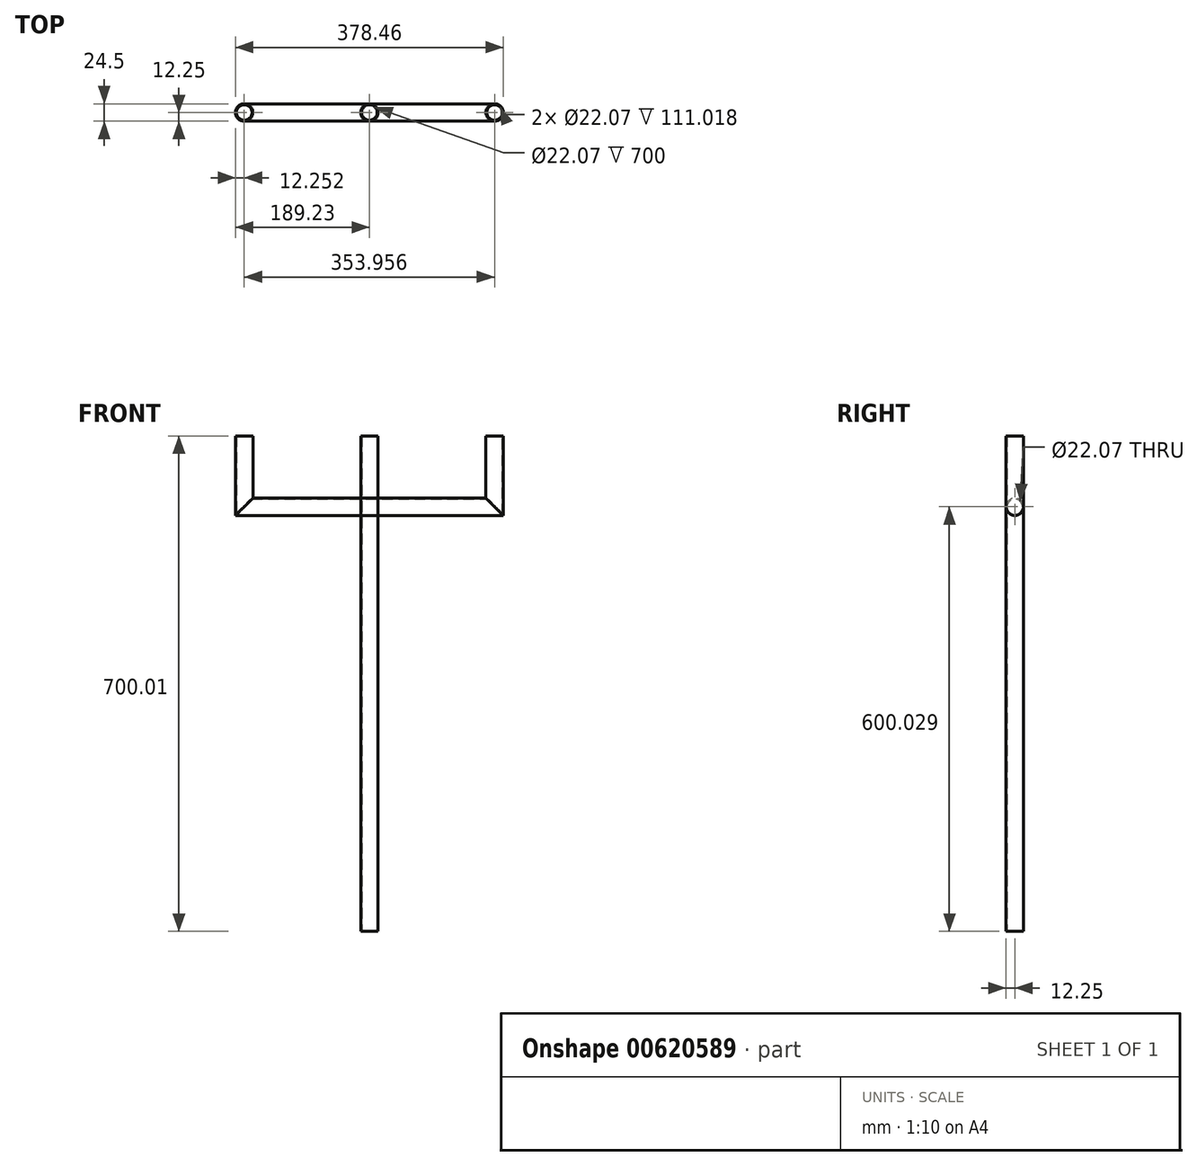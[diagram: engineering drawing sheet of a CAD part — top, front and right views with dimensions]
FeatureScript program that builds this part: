
annotation { "Feature Type Name" : "Feature", "Feature Type Description" : "" }
export const myFeature = defineFeature(function(context is Context, id is Id, definition is map)
    precondition{}
    {
        {
            var Q0;
            Q0=qCreatedBy(makeId("Top.planeOp"),FACE);
            var sketch = newSketch(context, id + "F0", { "sketchPlane" : qUnion([Q0])});
            skCircle(sketch, "E0", {"center": v(0, 0) * mm, "radius": 12.25 * mm});
            skCircle(sketch, "E1", {"center": v(0, 0) * mm, "radius": 11.03 * mm});
            skSolve(sketch);
        }
        {
            var Q0;
            Q0 = qSketchRegion(id + "F0", true);
            extrude(context, id + "F1", {"entities" : qUnion([Q0]), "depth" : 700 * mm, "offsetDistance" : 25 * mm});
        }
        {
            var Q0;
            Q0=qCreatedBy(makeId("Front.planeOp"),FACE);
            var sketch = newSketch(context, id + "F2", { "sketchPlane" : qUnion([Q0])});
            skLineSegment(sketch, "E2", {"start": v(0, 600) * mm, "end": v(177, 600) * mm});
            skLineSegment(sketch, "E3", {"start": v(177, 600) * mm, "end": v(177, 700) * mm});
            skLineSegment(sketch, "E4", {"start": v(0, 600) * mm, "end": v(-177, 600) * mm});
            skLineSegment(sketch, "E5", {"start": v(-177, 600) * mm, "end": v(-177, 700) * mm});
            skSolve(sketch);
        }
        {
            var Q0;
            Q0=qCreatedBy(makeId("Right.planeOp"),FACE);
            var sketch = newSketch(context, id + "F3", { "sketchPlane" : qUnion([Q0])});
            skCircle(sketch, "E6", {"center": v(0, 600.03) * mm, "radius": 12.25 * mm});
            skCircle(sketch, "E7", {"center": v(0, 600.03) * mm, "radius": 11.03 * mm});
            skSolve(sketch);
        }
        {
            var Q0;
            Q0=makeQuery(id+"F3.imprint","IMPRINT",FACE,{"disambiguationData":[TD([[makeQuery(id+"F3.imprint","IMPRINT",EDGE,{"derivedFrom":sQuery(id+"F3.wireOp",EDGE,"E6")}),1.0]])]});
            var Q1;
            Q1=sQuery(id+"F2.wireOp",EDGE,"E4");
            var Q2;
            Q2=sQuery(id+"F2.wireOp",EDGE,"E2");
            var Q3;
            Q3=sQuery(id+"F2.wireOp",EDGE,"E3");
            var Q4;
            Q4=sQuery(id+"F2.wireOp",EDGE,"E5");
            sweep(context, id + "F4", {"profiles" : qUnion([Q0]), "path" : qUnion([Q1, Q2, Q3, Q4])});
        }
    });
